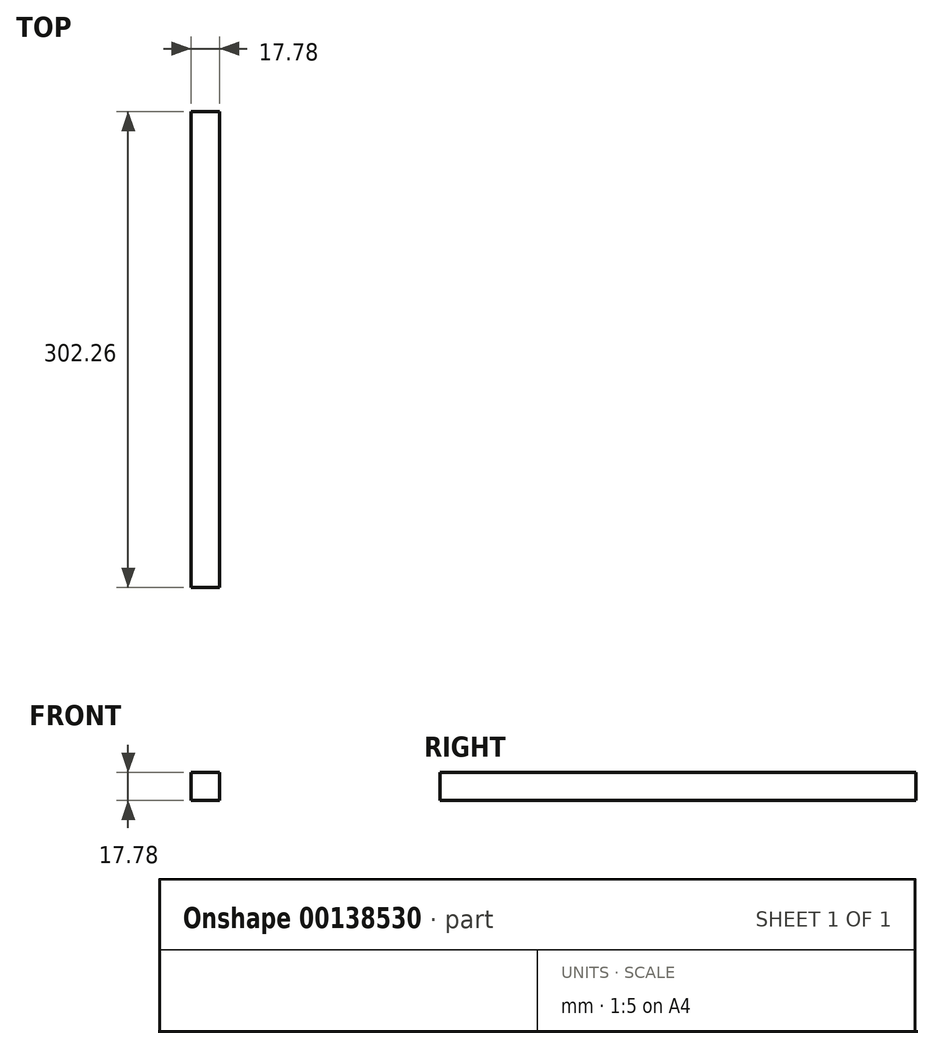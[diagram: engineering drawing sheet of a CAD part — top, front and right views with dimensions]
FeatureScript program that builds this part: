
annotation { "Feature Type Name" : "Feature", "Feature Type Description" : "" }
export const myFeature = defineFeature(function(context is Context, id is Id, definition is map)
    precondition{}
    {
        {
            var Q0;
            Q0=qCreatedBy(makeId("Top.planeOp"),FACE);
            var sketch = newSketch(context, id + "F0", { "sketchPlane" : qUnion([Q0])});
            skLineSegment(sketch, "E0.bottom", {"start": v(0, 0) * mm, "end": v(17.78, 0) * mm});
            skLineSegment(sketch, "E0.top", {"start": v(0, 302.26) * mm, "end": v(17.78, 302.26) * mm});
            skLineSegment(sketch, "E0.left", {"start": v(0, 0) * mm, "end": v(0, 302.26) * mm});
            skLineSegment(sketch, "E0.right", {"start": v(17.78, 0) * mm, "end": v(17.78, 302.26) * mm});
            skSolve(sketch);
        }
        {
            var Q0;
            Q0=makeQuery(id+"F0.imprint","IMPRINT",FACE,{"disambiguationData":[TD([[makeQuery(id+"F0.imprint","IMPRINT",EDGE,{"derivedFrom":sQuery(id+"F0.wireOp",EDGE,"E0.bottom")}),1.0]])]});
            extrude(context, id + "F1", {"entities" : qUnion([Q0]), "depth" : 17.78 * mm});
        }
    });
